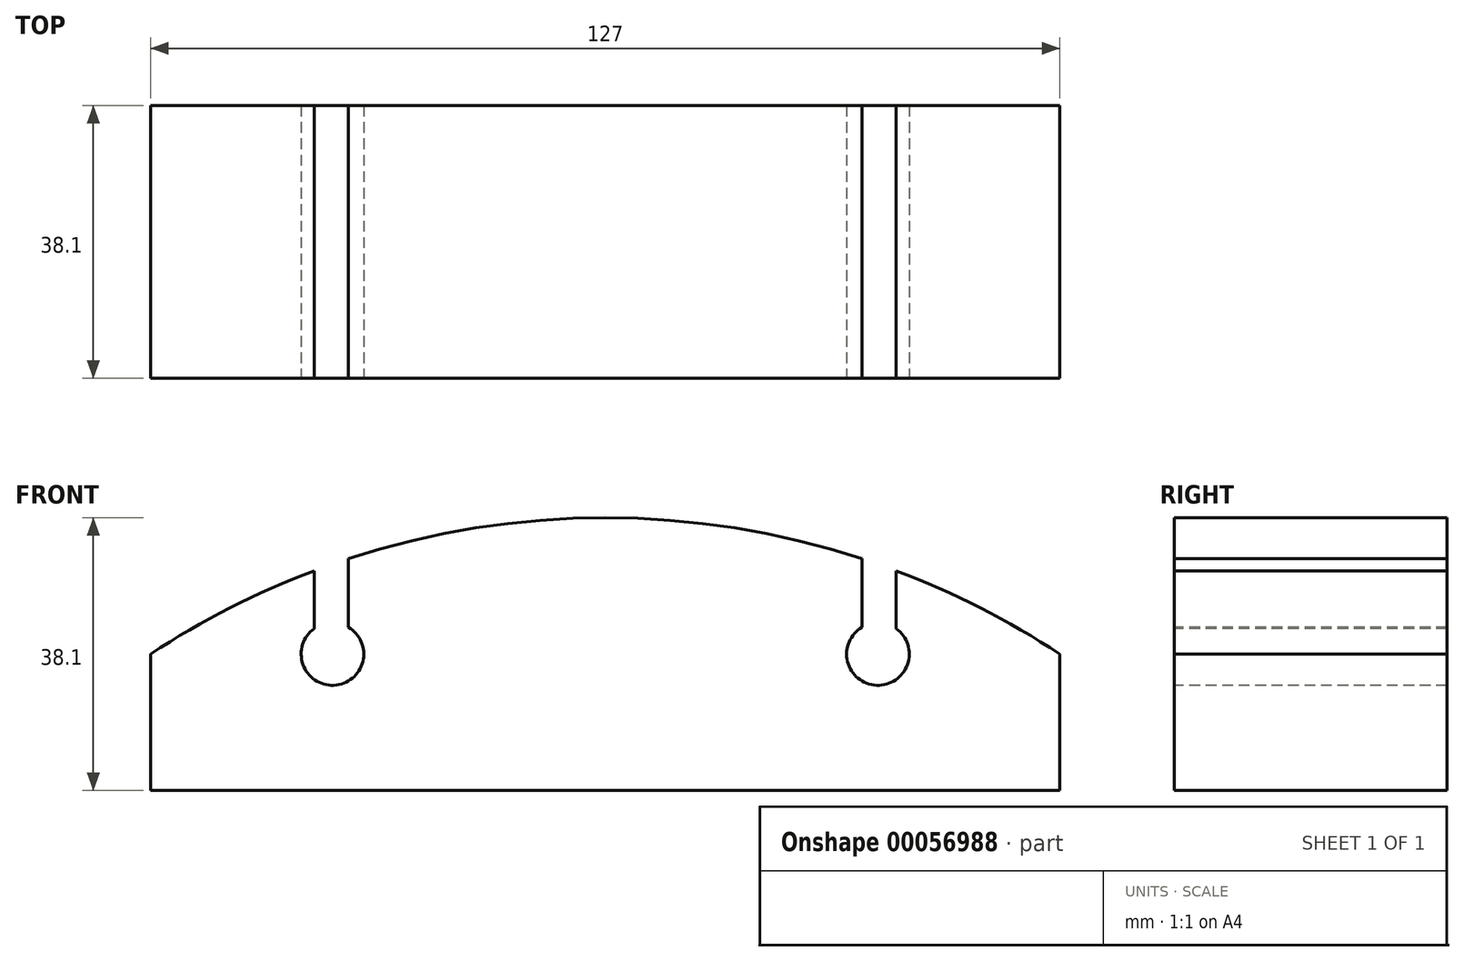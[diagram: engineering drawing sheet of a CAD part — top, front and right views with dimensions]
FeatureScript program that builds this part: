
annotation { "Feature Type Name" : "Feature", "Feature Type Description" : "" }
export const myFeature = defineFeature(function(context is Context, id is Id, definition is map)
    precondition{}
    {
        {
            var Q0;
            Q0=qCreatedBy(makeId("Front.planeOp"),FACE);
            var sketch = newSketch(context, id + "F0", { "sketchPlane" : qUnion([Q0])});
            skLineSegment(sketch, "E0.rect.bottom", {"start": v(63.5, -9.52) * mm, "end": v(-63.5, -9.53) * mm});
            skLineSegment(sketch, "E0.rect.left", {"start": v(63.5, -9.52) * mm, "end": v(63.5, 9.53) * mm});
            skLineSegment(sketch, "E0.rect.right", {"start": v(-63.5, -9.53) * mm, "end": v(-63.5, 9.52) * mm});
            skPoint(sketch, "E0.rect.middle", {"position": v(0, 0) * mm});
            skArc(sketch, "E1", {"start": v(63.5, 9.53) * mm, "mid": v(52.4, 15.99) * mm, "end": v(40.65, 21.17) * mm});
            skArc(sketch, "E2", {"start": v(35.88, 13.29) * mm, "mid": v(37.9, 5.16) * mm, "end": v(40.65, 13.07) * mm});
            skArc(sketch, "E3.MirrorC", {"start": v(-35.88, 13.29) * mm, "mid": v(-37.9, 5.16) * mm, "end": v(-40.65, 13.07) * mm});
            skLineSegment(sketch, "E4", {"start": v(35.88, 22.85) * mm, "end": v(35.88, 13.29) * mm});
            skLineSegment(sketch, "E5", {"start": v(40.65, 21.17) * mm, "end": v(40.65, 13.07) * mm});
            skLineSegment(sketch, "E6.MirrorCS", {"start": v(-35.88, 22.85) * mm, "end": v(-35.88, 13.29) * mm});
            skLineSegment(sketch, "E7.MirrorCS", {"start": v(-40.65, 21.17) * mm, "end": v(-40.65, 13.07) * mm});
            skArc(sketch, "E8.trimOffspring", {"start": v(-40.65, 21.17) * mm, "mid": v(-52.4, 15.99) * mm, "end": v(-63.5, 9.52) * mm});
            skArc(sketch, "E9.trimOffspring", {"start": v(35.88, 22.85) * mm, "mid": v(0, 28.57) * mm, "end": v(-35.88, 22.85) * mm});
            skSolve(sketch);
        }
        {
            var Q0;
            Q0=makeQuery(id+"F0.imprint","IMPRINT",FACE,{"disambiguationData":[TD([[makeQuery(id+"F0.imprint","IMPRINT",EDGE,{"derivedFrom":sQuery(id+"F0.wireOp",EDGE,"E0.rect.bottom")}),-1.0]])]});
            extrude(context, id + "F1", {"entities" : qUnion([Q0]), "oppositeDirection" : true, "depth" : 38.1 * mm});
        }
    });
